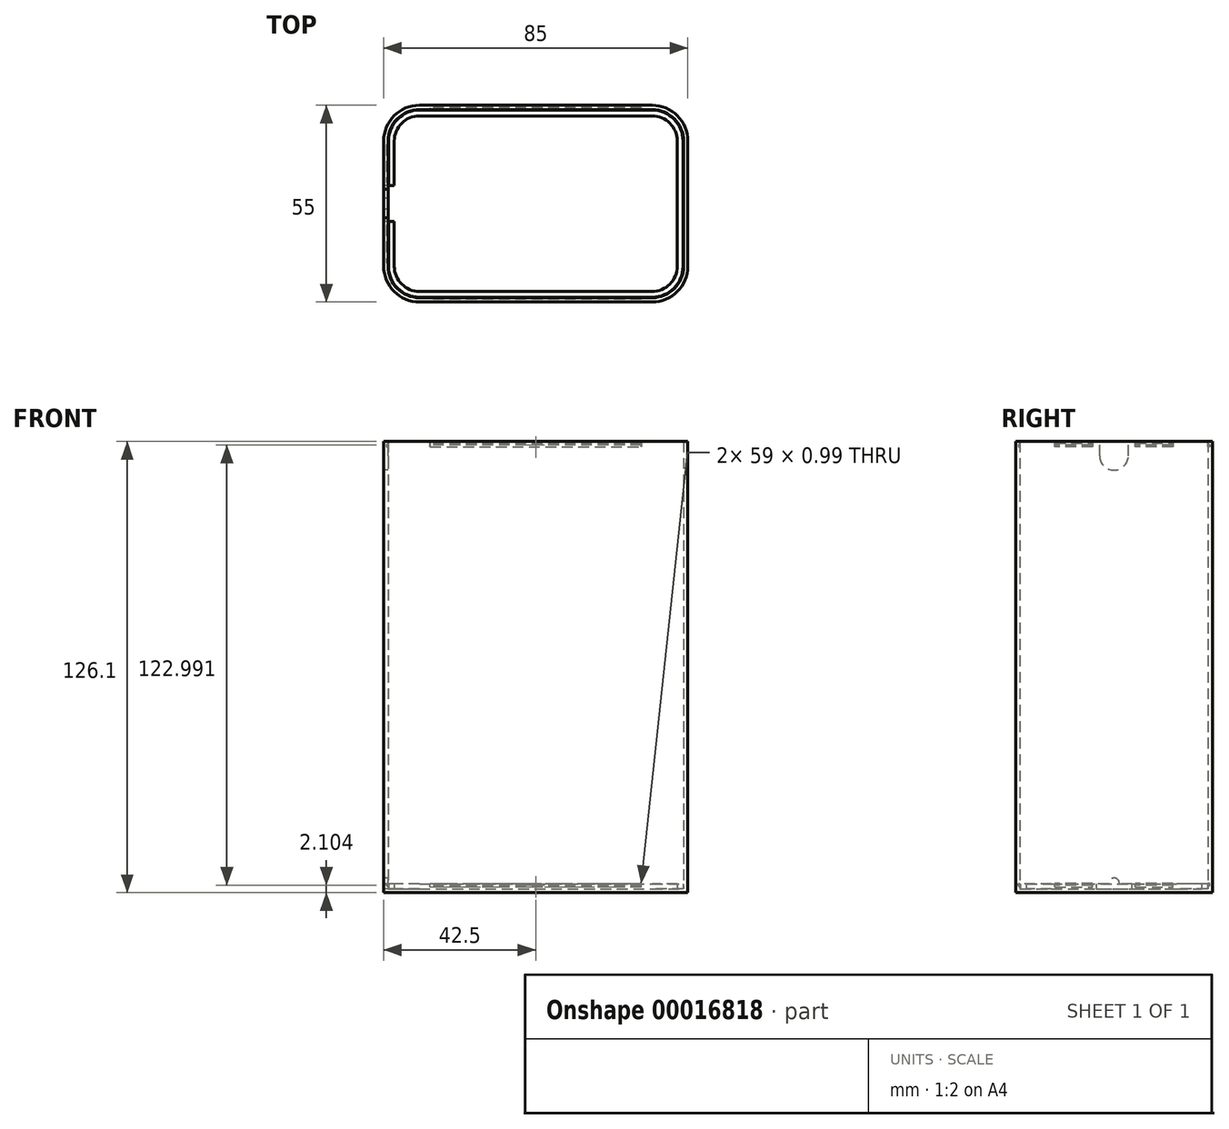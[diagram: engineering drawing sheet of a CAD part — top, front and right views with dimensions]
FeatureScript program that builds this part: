
annotation { "Feature Type Name" : "Feature", "Feature Type Description" : "" }
export const myFeature = defineFeature(function(context is Context, id is Id, definition is map)
    precondition{}
    {
        {
            var Q0;
            Q0=qCreatedBy(makeId("Top.planeOp"),FACE);
            var sketch = newSketch(context, id + "F0", { "sketchPlane" : qUnion([Q0])});
            skLineSegment(sketch, "E0.bottom", {"start": v(10, 0) * mm, "end": v(75, 0) * mm});
            skLineSegment(sketch, "E0.top", {"start": v(10, 55) * mm, "end": v(75, 55) * mm});
            skLineSegment(sketch, "E0.left", {"start": v(0, 10) * mm, "end": v(0, 45) * mm});
            skLineSegment(sketch, "E0.right", {"start": v(85, 10) * mm, "end": v(85, 45) * mm});
            skPoint(sketch, "E1.visualSharp", {"position": v(0, 55) * mm});
            skArc(sketch, "E1.filletArc", {"start": v(10, 55) * mm, "mid": v(2.93, 52.07) * mm, "end": v(0, 45) * mm});
            skPoint(sketch, "E2.visualSharp", {"position": v(0, 0) * mm});
            skArc(sketch, "E2.filletArc", {"start": v(0, 10) * mm, "mid": v(2.93, 2.93) * mm, "end": v(10, 0) * mm});
            skPoint(sketch, "E3.visualSharp", {"position": v(85, 0) * mm});
            skArc(sketch, "E3.filletArc", {"start": v(75, 0) * mm, "mid": v(82.07, 2.93) * mm, "end": v(85, 10) * mm});
            skPoint(sketch, "E4.visualSharp", {"position": v(85, 55) * mm});
            skArc(sketch, "E4.filletArc", {"start": v(85, 45) * mm, "mid": v(82.07, 52.07) * mm, "end": v(75, 55) * mm});
            skLineSegment(sketch, "E5.0", {"start": v(83.8, 10) * mm, "end": v(83.8, 45) * mm});
            skArc(sketch, "E5.1", {"start": v(75, 1.2) * mm, "mid": v(81.22, 3.78) * mm, "end": v(83.8, 10) * mm});
            skLineSegment(sketch, "E5.2", {"start": v(10, 1.2) * mm, "end": v(75, 1.2) * mm});
            skArc(sketch, "E5.3", {"start": v(1.2, 10) * mm, "mid": v(3.78, 3.78) * mm, "end": v(10, 1.2) * mm});
            skLineSegment(sketch, "E5.4", {"start": v(1.2, 10) * mm, "end": v(1.2, 45) * mm});
            skArc(sketch, "E5.5", {"start": v(83.8, 45) * mm, "mid": v(81.22, 51.22) * mm, "end": v(75, 53.8) * mm});
            skArc(sketch, "E5.6", {"start": v(10, 53.8) * mm, "mid": v(3.78, 51.22) * mm, "end": v(1.2, 45) * mm});
            skLineSegment(sketch, "E5.7", {"start": v(10, 53.8) * mm, "end": v(75, 53.8) * mm});
            skArc(sketch, "E6.0", {"start": v(10, 52.05) * mm, "mid": v(5.01, 49.99) * mm, "end": v(2.95, 45) * mm});
            skLineSegment(sketch, "E6.1", {"start": v(2.95, 10) * mm, "end": v(2.95, 45) * mm});
            skArc(sketch, "E6.2", {"start": v(2.95, 10) * mm, "mid": v(5.01, 5.01) * mm, "end": v(10, 2.95) * mm});
            skLineSegment(sketch, "E6.3", {"start": v(10, 2.95) * mm, "end": v(75, 2.95) * mm});
            skArc(sketch, "E6.4", {"start": v(75, 2.95) * mm, "mid": v(79.99, 5.01) * mm, "end": v(82.05, 10) * mm});
            skLineSegment(sketch, "E6.5", {"start": v(10, 52.05) * mm, "end": v(75, 52.05) * mm});
            skLineSegment(sketch, "E6.6", {"start": v(82.05, 10) * mm, "end": v(82.05, 45) * mm});
            skArc(sketch, "E6.7", {"start": v(82.05, 45) * mm, "mid": v(79.99, 49.99) * mm, "end": v(75, 52.05) * mm});
            skArc(sketch, "E7.0", {"start": v(10, 53.65) * mm, "mid": v(3.88, 51.12) * mm, "end": v(1.35, 45) * mm});
            skLineSegment(sketch, "E7.1", {"start": v(1.35, 10) * mm, "end": v(1.35, 45) * mm});
            skArc(sketch, "E7.2", {"start": v(1.35, 10) * mm, "mid": v(3.88, 3.88) * mm, "end": v(10, 1.35) * mm});
            skLineSegment(sketch, "E7.3", {"start": v(10, 1.35) * mm, "end": v(75, 1.35) * mm});
            skArc(sketch, "E7.4", {"start": v(75, 1.35) * mm, "mid": v(81.12, 3.88) * mm, "end": v(83.65, 10) * mm});
            skLineSegment(sketch, "E7.5", {"start": v(10, 53.65) * mm, "end": v(75, 53.65) * mm});
            skLineSegment(sketch, "E7.6", {"start": v(83.65, 10) * mm, "end": v(83.65, 45) * mm});
            skArc(sketch, "E7.7", {"start": v(83.65, 45) * mm, "mid": v(81.12, 51.12) * mm, "end": v(75, 53.65) * mm});
            skSolve(sketch);
        }
        {
            var Q0;
            Q0=makeQuery(id+"F0.imprint","IMPRINT",FACE,{"disambiguationData":[TD([[makeQuery(id+"F0.imprint","IMPRINT",EDGE,{"derivedFrom":sQuery(id+"F0.wireOp",EDGE,"E0.bottom")}),1.0]])]});
            extrude(context, id + "F1", {"entities" : qUnion([Q0]), "depth" : 125 * mm});
        }
        {
            var Q0;
            Q0=makeQuery(id+"F0.imprint","IMPRINT",FACE,{"disambiguationData":[TD([[makeQuery(id+"F0.imprint","IMPRINT",EDGE,{"derivedFrom":sQuery(id+"F0.wireOp",EDGE,"E5.0")}),1.0]])]});
            var Q1;
            Q1=makeQuery(id+"F0.imprint","IMPRINT",FACE,{"disambiguationData":[TD([[makeQuery(id+"F0.imprint","IMPRINT",EDGE,{"derivedFrom":sQuery(id+"F0.wireOp",EDGE,"E0.bottom")}),1.0]])]});
            var Q2;
            Q2=makeQuery(id+"F0.imprint","IMPRINT",FACE,{"disambiguationData":[TD([[makeQuery(id+"F0.imprint","IMPRINT",EDGE,{"derivedFrom":sQuery(id+"F0.wireOp",EDGE,"E6.0")}),1.0]])]});
            var Q3;
            Q3=makeQuery(id+"F0.imprint","IMPRINT",FACE,{"disambiguationData":[TD([[makeQuery(id+"F0.imprint","IMPRINT",EDGE,{"derivedFrom":sQuery(id+"F0.wireOp",EDGE,"E6.0")}),-1.0]])]});
            extrude(context, id + "F2", {"entities" : qUnion([Q0, Q1, Q2, Q3]), "oppositeDirection" : true, "depth" : 1.1 * mm});
        }
        {
            var Q0;
            Q0=makeQuery(id+"F0.imprint","IMPRINT",FACE,{"disambiguationData":[TD([[makeQuery(id+"F0.imprint","IMPRINT",EDGE,{"derivedFrom":sQuery(id+"F0.wireOp",EDGE,"E6.0")}),-1.0]])]});
            extrude(context, id + "F3", {"entities" : qUnion([Q0]), "operationType" : NewBodyOperationType.ADD, "depth" : 1.4 * mm});
        }
        {
            var Q0;
            Q0=makeQuery(id+"F1.opExtrude","SWEPT_FACE",FACE,{"disambiguationData":[OSD([sQuery(id+"F0.wireOp",EDGE,"E0.left")])]});
            var sketch = newSketch(context, id + "F4", { "sketchPlane" : qUnion([Q0])});
            skLineSegment(sketch, "E8.0", {"start": v(-10, 125) * mm, "end": v(-45, 125) * mm, "construction": true});
            skLineSegment(sketch, "E9.0", {"start": v(-10, 0) * mm, "end": v(-45, 0) * mm, "construction": true});
            skLineSegment(sketch, "E10", {"start": v(-27.5, 125) * mm, "end": v(-27.5, 0) * mm, "construction": true});
            skCircle(sketch, "E11", {"center": v(-27.5, 121) * mm, "radius": 4 * mm});
            skCircle(sketch, "E12", {"center": v(-27.5, 1.5) * mm, "radius": 1.5 * mm});
            skLineSegment(sketch, "E13", {"start": v(-23.5, 121) * mm, "end": v(-23.5, 125) * mm});
            skLineSegment(sketch, "E14", {"start": v(-31.5, 121) * mm, "end": v(-31.5, 125) * mm});
            skLineSegment(sketch, "E15", {"start": v(-26, 1.5) * mm, "end": v(-26, 0) * mm});
            skLineSegment(sketch, "E16", {"start": v(-29, 1.5) * mm, "end": v(-29, 0) * mm});
            skLineSegment(sketch, "E17.0", {"start": v(-53.65, 1.4) * mm, "end": v(-53.65, 0) * mm, "construction": true});
            skLineSegment(sketch, "E18.0", {"start": v(-55, 0) * mm, "end": v(-45, 0) * mm, "construction": true});
            skLineSegment(sketch, "E19", {"start": v(-53.65, 0.5) * mm, "end": v(-54.15, 1) * mm});
            skLineSegment(sketch, "E20", {"start": v(-54.15, 1) * mm, "end": v(-54.15, 1.4) * mm});
            skLineSegment(sketch, "E21", {"start": v(-54.15, 1.4) * mm, "end": v(-53.65, 1.4) * mm});
            skLineSegment(sketch, "E22.0", {"start": v(-54.25, 1.5) * mm, "end": v(-53.65, 1.5) * mm});
            skLineSegment(sketch, "E22.1", {"start": v(-54.25, 0.96) * mm, "end": v(-54.25, 1.5) * mm});
            skLineSegment(sketch, "E22.2", {"start": v(-53.65, 0.36) * mm, "end": v(-54.25, 0.96) * mm});
            skLineSegment(sketch, "E23", {"start": v(-53.65, 1.5) * mm, "end": v(-53.65, 0.36) * mm});
            skLineSegment(sketch, "E24.MirrorCS", {"start": v(-0.75, 0.96) * mm, "end": v(-0.75, 1.5) * mm});
            skLineSegment(sketch, "E25.MirrorCS", {"start": v(-1.35, 0.5) * mm, "end": v(-0.85, 1) * mm});
            skLineSegment(sketch, "E26.MirrorCS", {"start": v(-0.85, 1) * mm, "end": v(-0.85, 1.4) * mm});
            skLineSegment(sketch, "E27.MirrorCS", {"start": v(-1.35, 0.36) * mm, "end": v(-0.75, 0.96) * mm});
            skLineSegment(sketch, "E28.MirrorCS", {"start": v(-0.75, 1.5) * mm, "end": v(-1.35, 1.5) * mm});
            skLineSegment(sketch, "E29.MirrorCS", {"start": v(-0.85, 1.4) * mm, "end": v(-1.35, 1.4) * mm});
            skLineSegment(sketch, "E30.MirrorCS", {"start": v(-1.35, 1.5) * mm, "end": v(-1.35, 0.36) * mm});
            skLineSegment(sketch, "E31", {"start": v(-45.1, 62.5) * mm, "end": v(-10, 62.5) * mm, "construction": true});
            skPoint(sketch, "E32.orphan", {"position": v(-27.5, 62.5) * mm});
            skLineSegment(sketch, "E33.MirrorCS", {"start": v(-0.75, 124.04) * mm, "end": v(-0.75, 123.5) * mm});
            skLineSegment(sketch, "E34.MirrorCS", {"start": v(-0.85, 124) * mm, "end": v(-0.85, 123.6) * mm});
            skLineSegment(sketch, "E35.MirrorCS", {"start": v(-1.35, 123.5) * mm, "end": v(-1.35, 124.64) * mm});
            skLineSegment(sketch, "E36.MirrorCS", {"start": v(-0.85, 123.6) * mm, "end": v(-1.35, 123.6) * mm});
            skLineSegment(sketch, "E37.MirrorCS", {"start": v(-1.35, 124.5) * mm, "end": v(-0.85, 124) * mm});
            skLineSegment(sketch, "E38.MirrorCS", {"start": v(-1.35, 124.64) * mm, "end": v(-0.75, 124.04) * mm});
            skLineSegment(sketch, "E39.MirrorCS", {"start": v(-0.75, 123.5) * mm, "end": v(-1.35, 123.5) * mm});
            skLineSegment(sketch, "E40.MirrorCS", {"start": v(-54.25, 123.5) * mm, "end": v(-53.65, 123.5) * mm});
            skLineSegment(sketch, "E41.MirrorCS", {"start": v(-53.65, 124.64) * mm, "end": v(-54.25, 124.04) * mm});
            skLineSegment(sketch, "E42.MirrorCS", {"start": v(-54.25, 124.04) * mm, "end": v(-54.25, 123.5) * mm});
            skLineSegment(sketch, "E43.MirrorCS", {"start": v(-54.15, 123.6) * mm, "end": v(-53.65, 123.6) * mm});
            skLineSegment(sketch, "E44.MirrorCS", {"start": v(-53.65, 124.5) * mm, "end": v(-54.15, 124) * mm});
            skLineSegment(sketch, "E45.MirrorCS", {"start": v(-53.65, 123.5) * mm, "end": v(-53.65, 124.64) * mm});
            skLineSegment(sketch, "E46.MirrorCS", {"start": v(-54.15, 124) * mm, "end": v(-54.15, 123.6) * mm});
            skLineSegment(sketch, "E47", {"start": v(-32.5, 0) * mm, "end": v(-32.5, 1.4) * mm});
            skLineSegment(sketch, "E48", {"start": v(-32.5, 1.4) * mm, "end": v(-22.5, 1.4) * mm});
            skLineSegment(sketch, "E49", {"start": v(-22.5, 1.4) * mm, "end": v(-22.5, 0) * mm});
            skSolve(sketch);
        }
        {
            var Q0;
            {var subQ0=sQuery(id+"F4.wireOp",EDGE,"E11");var subQ2=makeQuery(id+"F4.imprint","INTERSECT",VERTEX,{"derivedFrom":[subQ0,sQuery(id+"F4.wireOp",EDGE,"E13")]});Q0=makeQuery(id+"F4.imprint","IMPRINT",FACE,{"disambiguationData":[TD([[makeQuery(id+"F4.imprint","IMPRINT",EDGE,{"disambiguationData":[TD([[subQ2,-1.0]])],"derivedFrom":subQ0}),1.0]])]});}
            var Q1;
            {var subQ3=sQuery(id+"F4.wireOp",EDGE,"E13");Q1=makeQuery(id+"F4.imprint","IMPRINT",FACE,{"disambiguationData":[TD([[makeQuery(id+"F4.imprint","IMPRINT",EDGE,{"derivedFrom":subQ3}),1.0]])]});}
            var Q2;
            {var subQ3=sQuery(id+"F4.wireOp",EDGE,"E14");Q2=makeQuery(id+"F4.imprint","IMPRINT",FACE,{"disambiguationData":[TD([[makeQuery(id+"F4.imprint","IMPRINT",EDGE,{"derivedFrom":subQ3}),-1.0]])]});}
            var Q3;
            {var subQ0=sQuery(id+"F4.wireOp",EDGE,"E12");var subQ2=makeQuery(id+"F4.imprint","INTERSECT",VERTEX,{"derivedFrom":[subQ0,sQuery(id+"F4.wireOp",EDGE,"E15")]});Q3=makeQuery(id+"F4.imprint","IMPRINT",FACE,{"disambiguationData":[TD([[makeQuery(id+"F4.imprint","IMPRINT",EDGE,{"disambiguationData":[TD([[subQ2,-1.0]])],"derivedFrom":subQ0}),1.0]])]});}
            var Q4;
            {var subQ3=sQuery(id+"F4.wireOp",EDGE,"E15");Q4=makeQuery(id+"F4.imprint","IMPRINT",FACE,{"disambiguationData":[TD([[makeQuery(id+"F4.imprint","IMPRINT",EDGE,{"derivedFrom":subQ3}),-1.0]])]});}
            var Q5;
            {var subQ3=sQuery(id+"F4.wireOp",EDGE,"E16");Q5=makeQuery(id+"F4.imprint","IMPRINT",FACE,{"disambiguationData":[TD([[makeQuery(id+"F4.imprint","IMPRINT",EDGE,{"derivedFrom":subQ3}),1.0]])]});}
            var Q6;
            {var subQ1=sQuery(id+"F4.wireOp",EDGE,"E12");var subQ5=sQuery(id+"F4.wireOp",EDGE,"E48");var subQ7=makeQuery(id+"F4.imprint","INTERSECT",VERTEX,{"disambiguationData":[OD(0.0)],"derivedFrom":[subQ1,subQ5]});Q6=makeQuery(id+"F4.imprint","IMPRINT",FACE,{"disambiguationData":[TD([[makeQuery(id+"F4.imprint","IMPRINT",EDGE,{"disambiguationData":[TD([[subQ7,-1.0]])],"derivedFrom":subQ1}),-1.0]])]});}
            var Q7;
            {var subQ1=sQuery(id+"F4.wireOp",EDGE,"E12");var subQ5=sQuery(id+"F4.wireOp",EDGE,"E48");var subQ7=makeQuery(id+"F4.imprint","INTERSECT",VERTEX,{"disambiguationData":[OD(1.0)],"derivedFrom":[subQ1,subQ5]});Q7=makeQuery(id+"F4.imprint","IMPRINT",FACE,{"disambiguationData":[TD([[makeQuery(id+"F4.imprint","IMPRINT",EDGE,{"disambiguationData":[TD([[subQ7,1.0]])],"derivedFrom":subQ1}),-1.0]])]});}
            var Q8;
            {var subQ0=sQuery(id+"F4.wireOp",EDGE,"E48");var subQ1=sQuery(id+"F4.wireOp",EDGE,"E12");var subQ3=makeQuery(id+"F4.imprint","INTERSECT",VERTEX,{"disambiguationData":[OD(0.0)],"derivedFrom":[subQ1,subQ0]});Q8=makeQuery(id+"F4.imprint","IMPRINT",FACE,{"disambiguationData":[TD([[makeQuery(id+"F4.imprint","IMPRINT",EDGE,{"disambiguationData":[TD([[subQ3,-1.0]])],"derivedFrom":subQ1}),1.0]])]});}
            extrude(context, id + "F5", {"entities" : qUnion([Q0, Q1, Q2, Q3, Q4, Q5, Q6, Q7, Q8]), "operationType" : NewBodyOperationType.REMOVE, "oppositeDirection" : true, "depth" : 1.2 * mm});
        }
        {
            var Q0;
            {var subQ2=sQuery(id+"F4.wireOp",EDGE,"E19");Q0=makeQuery(id+"F4.imprint","IMPRINT",FACE,{"disambiguationData":[TD([[makeQuery(id+"F4.imprint","IMPRINT",EDGE,{"derivedFrom":subQ2}),-1.0]])]});}
            var Q1;
            {var subQ2=sQuery(id+"F4.wireOp",EDGE,"E25.MirrorCS");Q1=makeQuery(id+"F4.imprint","IMPRINT",FACE,{"disambiguationData":[TD([[makeQuery(id+"F4.imprint","IMPRINT",EDGE,{"derivedFrom":subQ2}),1.0]])]});}
            extrude(context, id + "F6", {"entities" : qUnion([Q0, Q1]), "operationType" : NewBodyOperationType.ADD, "oppositeDirection" : true, "depth" : 70 * mm, "hasSecondDirection" : true, "secondDirectionOppositeDirection" : true, "secondDirectionDepth" : 15 * mm});
        }
        {
            var Q0;
            {var subQ2=sQuery(id+"F4.wireOp",EDGE,"E19");Q0=makeQuery(id+"F4.imprint","IMPRINT",FACE,{"disambiguationData":[TD([[makeQuery(id+"F4.imprint","IMPRINT",EDGE,{"derivedFrom":subQ2}),-1.0]])]});}
            var Q1;
            {var subQ2=sQuery(id+"F4.wireOp",EDGE,"E19");Q1=makeQuery(id+"F4.imprint","IMPRINT",FACE,{"disambiguationData":[TD([[makeQuery(id+"F4.imprint","IMPRINT",EDGE,{"derivedFrom":subQ2}),1.0]])]});}
            var Q2;
            {var subQ2=sQuery(id+"F4.wireOp",EDGE,"E25.MirrorCS");Q2=makeQuery(id+"F4.imprint","IMPRINT",FACE,{"disambiguationData":[TD([[makeQuery(id+"F4.imprint","IMPRINT",EDGE,{"derivedFrom":subQ2}),1.0]])]});}
            var Q3;
            Q3=makeQuery(id+"F4.imprint","IMPRINT",FACE,{"disambiguationData":[TD([[makeQuery(id+"F4.imprint","IMPRINT",EDGE,{"derivedFrom":sQuery(id+"F4.wireOp",EDGE,"E24.MirrorCS")}),1.0]])]});
            var Q4;
            {var subQ4=sQuery(id+"F4.wireOp",EDGE,"E40.MirrorCS");Q4=makeQuery(id+"F4.imprint","IMPRINT",FACE,{"disambiguationData":[TD([[makeQuery(id+"F4.imprint","IMPRINT",EDGE,{"derivedFrom":subQ4}),1.0]])]});}
            var Q5;
            {var subQ2=sQuery(id+"F4.wireOp",EDGE,"E43.MirrorCS");Q5=makeQuery(id+"F4.imprint","IMPRINT",FACE,{"disambiguationData":[TD([[makeQuery(id+"F4.imprint","IMPRINT",EDGE,{"derivedFrom":subQ2}),1.0]])]});}
            var Q6;
            Q6=makeQuery(id+"F4.imprint","IMPRINT",FACE,{"disambiguationData":[TD([[makeQuery(id+"F4.imprint","IMPRINT",EDGE,{"derivedFrom":sQuery(id+"F4.wireOp",EDGE,"E34.MirrorCS")}),-1.0]])]});
            var Q7;
            Q7=makeQuery(id+"F4.imprint","IMPRINT",FACE,{"disambiguationData":[TD([[makeQuery(id+"F4.imprint","IMPRINT",EDGE,{"derivedFrom":sQuery(id+"F4.wireOp",EDGE,"E33.MirrorCS")}),-1.0]])]});
            extrude(context, id + "F7", {"entities" : qUnion([Q0, Q1, Q2, Q3, Q4, Q5, Q6, Q7]), "operationType" : NewBodyOperationType.REMOVE, "oppositeDirection" : true, "depth" : 72 * mm, "hasSecondDirection" : true, "secondDirectionOppositeDirection" : true, "secondDirectionDepth" : 13 * mm});
        }
        {
            var Q0;
            {var subQ1=sQuery(id+"F4.wireOp",EDGE,"E47");Q0=makeQuery(id+"F4.imprint","IMPRINT",FACE,{"disambiguationData":[TD([[makeQuery(id+"F4.imprint","IMPRINT",EDGE,{"derivedFrom":subQ1}),-1.0]])]});}
            var Q1;
            {var subQ1=sQuery(id+"F4.wireOp",EDGE,"E12");var subQ5=sQuery(id+"F4.wireOp",EDGE,"E48");var subQ7=makeQuery(id+"F4.imprint","INTERSECT",VERTEX,{"disambiguationData":[OD(0.0)],"derivedFrom":[subQ1,subQ5]});Q1=makeQuery(id+"F4.imprint","IMPRINT",FACE,{"disambiguationData":[TD([[makeQuery(id+"F4.imprint","IMPRINT",EDGE,{"disambiguationData":[TD([[subQ7,-1.0]])],"derivedFrom":subQ1}),-1.0]])]});}
            var Q2;
            {var subQ1=sQuery(id+"F4.wireOp",EDGE,"E12");var subQ5=sQuery(id+"F4.wireOp",EDGE,"E48");var subQ7=makeQuery(id+"F4.imprint","INTERSECT",VERTEX,{"disambiguationData":[OD(1.0)],"derivedFrom":[subQ1,subQ5]});Q2=makeQuery(id+"F4.imprint","IMPRINT",FACE,{"disambiguationData":[TD([[makeQuery(id+"F4.imprint","IMPRINT",EDGE,{"disambiguationData":[TD([[subQ7,1.0]])],"derivedFrom":subQ1}),-1.0]])]});}
            var Q3;
            {var subQ0=sQuery(id+"F4.wireOp",EDGE,"E49");Q3=makeQuery(id+"F4.imprint","IMPRINT",FACE,{"disambiguationData":[TD([[makeQuery(id+"F4.imprint","IMPRINT",EDGE,{"derivedFrom":subQ0}),-1.0]])]});}
            var Q4;
            {var subQ0=sQuery(id+"F4.wireOp",EDGE,"E48");var subQ1=sQuery(id+"F4.wireOp",EDGE,"E12");var subQ3=makeQuery(id+"F4.imprint","INTERSECT",VERTEX,{"disambiguationData":[OD(0.0)],"derivedFrom":[subQ1,subQ0]});Q4=makeQuery(id+"F4.imprint","IMPRINT",FACE,{"disambiguationData":[TD([[makeQuery(id+"F4.imprint","IMPRINT",EDGE,{"disambiguationData":[TD([[subQ3,-1.0]])],"derivedFrom":subQ1}),1.0]])]});}
            extrude(context, id + "F8", {"entities" : qUnion([Q0, Q1, Q2, Q3, Q4]), "operationType" : NewBodyOperationType.REMOVE, "oppositeDirection" : true, "depth" : 4 * mm});
        }
        {
            var Q0;
            Q0=makeQuery(id+"F1.opExtrude","SWEPT_FACE",FACE,{"disambiguationData":[OSD([sQuery(id+"F0.wireOp",EDGE,"E0.bottom")])]});
            var sketch = newSketch(context, id + "F9", { "sketchPlane" : qUnion([Q0])});
            skLineSegment(sketch, "E50", {"start": v(0.85, 1.4) * mm, "end": v(1.35, 1.4) * mm});
            skLineSegment(sketch, "E51.0", {"start": v(0.75, 1.5) * mm, "end": v(1.35, 1.5) * mm});
            skLineSegment(sketch, "E51.1", {"start": v(0.75, 0.96) * mm, "end": v(0.75, 1.5) * mm});
            skLineSegment(sketch, "E51.2", {"start": v(1.35, 0.36) * mm, "end": v(0.75, 0.96) * mm});
            skLineSegment(sketch, "E52", {"start": v(1.35, 0.5) * mm, "end": v(0.85, 1) * mm});
            skLineSegment(sketch, "E53.0", {"start": v(1.35, 1.4) * mm, "end": v(1.35, 0) * mm, "construction": true});
            skLineSegment(sketch, "E54", {"start": v(0.85, 1) * mm, "end": v(0.85, 1.4) * mm});
            skLineSegment(sketch, "E55", {"start": v(1.35, 1.5) * mm, "end": v(1.35, 0.36) * mm});
            skPoint(sketch, "E56.0", {"position": v(1.35, 0) * mm});
            skLineSegment(sketch, "E57.0", {"start": v(0, 125) * mm, "end": v(0, 0) * mm, "construction": true});
            skLineSegment(sketch, "E58", {"start": v(0, 62.5) * mm, "end": v(37.76, 62.5) * mm, "construction": true});
            skLineSegment(sketch, "E59.MirrorCS", {"start": v(0.85, 123.6) * mm, "end": v(1.35, 123.6) * mm});
            skLineSegment(sketch, "E60.MirrorCS", {"start": v(0.75, 124.04) * mm, "end": v(0.75, 123.5) * mm});
            skLineSegment(sketch, "E61.MirrorCS", {"start": v(0.75, 123.5) * mm, "end": v(1.35, 123.5) * mm});
            skLineSegment(sketch, "E62.MirrorCS", {"start": v(1.35, 124.64) * mm, "end": v(0.75, 124.04) * mm});
            skLineSegment(sketch, "E63.MirrorCS", {"start": v(1.35, 124.5) * mm, "end": v(0.85, 124) * mm});
            skLineSegment(sketch, "E64.MirrorCS", {"start": v(0.85, 124) * mm, "end": v(0.85, 123.6) * mm});
            skLineSegment(sketch, "E65.MirrorCS", {"start": v(1.35, 123.5) * mm, "end": v(1.35, 124.64) * mm});
            skSolve(sketch);
        }
        {
            var Q0;
            {var subQ2=sQuery(id+"F9.wireOp",EDGE,"E50");Q0=makeQuery(id+"F9.imprint","IMPRINT",FACE,{"disambiguationData":[TD([[makeQuery(id+"F9.imprint","IMPRINT",EDGE,{"derivedFrom":subQ2}),-1.0]])]});}
            extrude(context, id + "F10", {"entities" : qUnion([Q0]), "operationType" : NewBodyOperationType.ADD, "oppositeDirection" : true, "depth" : 20.5 * mm, "hasSecondDirection" : true, "secondDirectionOppositeDirection" : true, "secondDirectionDepth" : 12 * mm});
        }
        {
            var Q0;
            {var subQ2=sQuery(id+"F9.wireOp",EDGE,"E50");Q0=makeQuery(id+"F9.imprint","IMPRINT",FACE,{"disambiguationData":[TD([[makeQuery(id+"F9.imprint","IMPRINT",EDGE,{"derivedFrom":subQ2}),-1.0]])]});}
            extrude(context, id + "F11", {"entities" : qUnion([Q0]), "operationType" : NewBodyOperationType.ADD, "oppositeDirection" : true, "depth" : 43 * mm, "hasSecondDirection" : true, "secondDirectionOppositeDirection" : true, "secondDirectionDepth" : 34.5 * mm});
        }
        {
            var Q0;
            {var subQ2=sQuery(id+"F9.wireOp",EDGE,"E50");Q0=makeQuery(id+"F9.imprint","IMPRINT",FACE,{"disambiguationData":[TD([[makeQuery(id+"F9.imprint","IMPRINT",EDGE,{"derivedFrom":subQ2}),-1.0]])]});}
            var Q1;
            {var subQ2=sQuery(id+"F9.wireOp",EDGE,"E50");Q1=makeQuery(id+"F9.imprint","IMPRINT",FACE,{"disambiguationData":[TD([[makeQuery(id+"F9.imprint","IMPRINT",EDGE,{"derivedFrom":subQ2}),1.0]])]});}
            var Q2;
            {var subQ4=sQuery(id+"F9.wireOp",EDGE,"E59.MirrorCS");Q2=makeQuery(id+"F9.imprint","IMPRINT",FACE,{"disambiguationData":[TD([[makeQuery(id+"F9.imprint","IMPRINT",EDGE,{"derivedFrom":subQ4}),-1.0]])]});}
            var Q3;
            {var subQ2=sQuery(id+"F9.wireOp",EDGE,"E59.MirrorCS");Q3=makeQuery(id+"F9.imprint","IMPRINT",FACE,{"disambiguationData":[TD([[makeQuery(id+"F9.imprint","IMPRINT",EDGE,{"derivedFrom":subQ2}),1.0]])]});}
            extrude(context, id + "F12", {"entities" : qUnion([Q0, Q1, Q2, Q3]), "operationType" : NewBodyOperationType.REMOVE, "oppositeDirection" : true, "depth" : 21.5 * mm, "hasSecondDirection" : true, "secondDirectionOppositeDirection" : true, "secondDirectionDepth" : 11 * mm});
        }
        {
            var Q0;
            {var subQ2=sQuery(id+"F9.wireOp",EDGE,"E50");Q0=makeQuery(id+"F9.imprint","IMPRINT",FACE,{"disambiguationData":[TD([[makeQuery(id+"F9.imprint","IMPRINT",EDGE,{"derivedFrom":subQ2}),-1.0]])]});}
            var Q1;
            {var subQ2=sQuery(id+"F9.wireOp",EDGE,"E50");Q1=makeQuery(id+"F9.imprint","IMPRINT",FACE,{"disambiguationData":[TD([[makeQuery(id+"F9.imprint","IMPRINT",EDGE,{"derivedFrom":subQ2}),1.0]])]});}
            var Q2;
            {var subQ4=sQuery(id+"F9.wireOp",EDGE,"E59.MirrorCS");Q2=makeQuery(id+"F9.imprint","IMPRINT",FACE,{"disambiguationData":[TD([[makeQuery(id+"F9.imprint","IMPRINT",EDGE,{"derivedFrom":subQ4}),-1.0]])]});}
            var Q3;
            {var subQ2=sQuery(id+"F9.wireOp",EDGE,"E59.MirrorCS");Q3=makeQuery(id+"F9.imprint","IMPRINT",FACE,{"disambiguationData":[TD([[makeQuery(id+"F9.imprint","IMPRINT",EDGE,{"derivedFrom":subQ2}),1.0]])]});}
            extrude(context, id + "F13", {"entities" : qUnion([Q0, Q1, Q2, Q3]), "operationType" : NewBodyOperationType.REMOVE, "oppositeDirection" : true, "depth" : 44 * mm, "hasSecondDirection" : true, "secondDirectionOppositeDirection" : true, "secondDirectionDepth" : 33.5 * mm});
        }
    });
